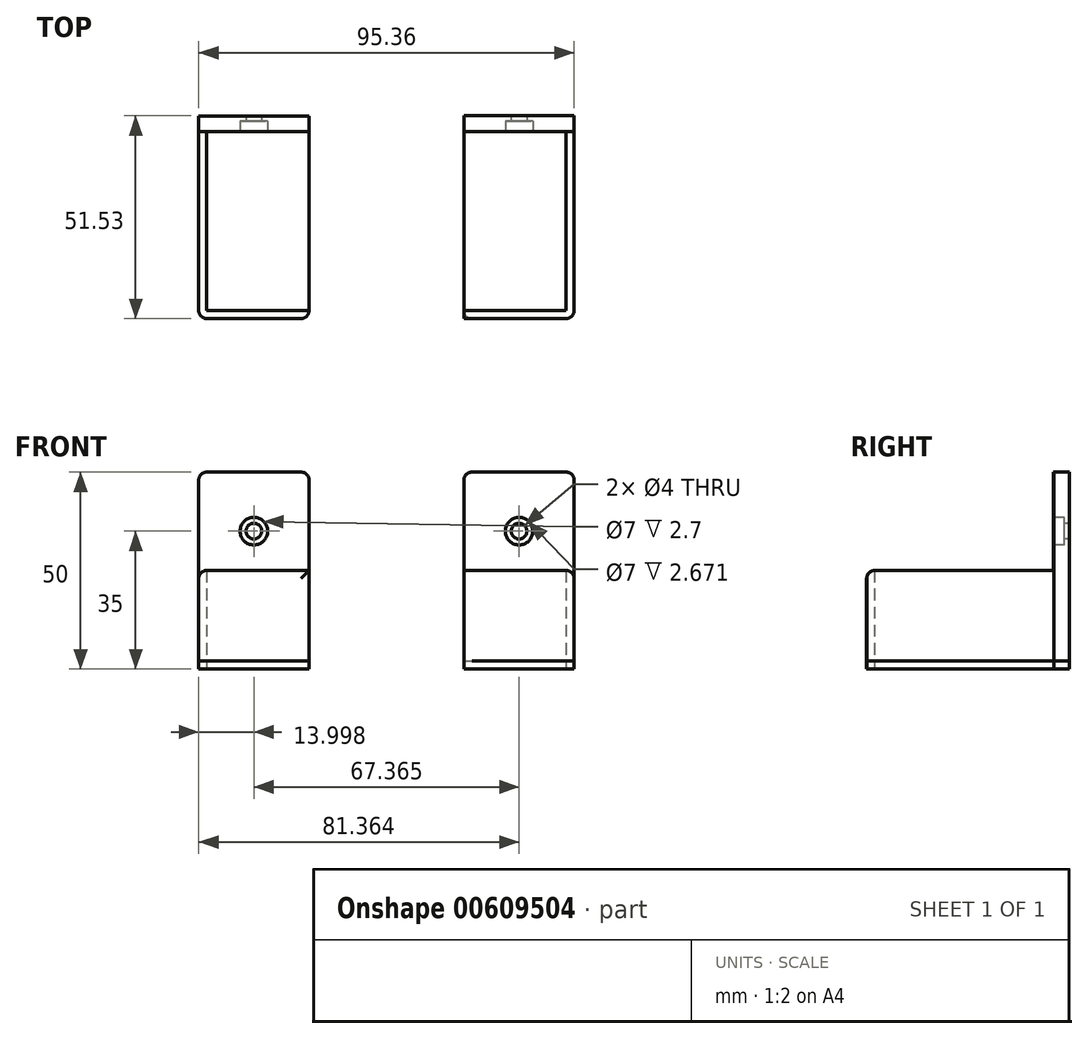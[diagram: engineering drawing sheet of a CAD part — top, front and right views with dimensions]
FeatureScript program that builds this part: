
annotation { "Feature Type Name" : "Feature", "Feature Type Description" : "" }
export const myFeature = defineFeature(function(context is Context, id is Id, definition is map)
    precondition{}
    {
        {
            var Q0;
            Q0=qCreatedBy(makeId("Top.planeOp"),FACE);
            var sketch = newSketch(context, id + "F0", { "sketchPlane" : qUnion([Q0])});
            skLineSegment(sketch, "E0.bottom", {"start": v(17.3, 23.4) * mm, "end": v(45.3, 23.4) * mm});
            skLineSegment(sketch, "E0.top", {"start": v(17.3, -28.1) * mm, "end": v(45.3, -28.1) * mm});
            skLineSegment(sketch, "E0.left", {"start": v(17.3, 23.4) * mm, "end": v(17.3, -28.1) * mm});
            skLineSegment(sketch, "E0.right", {"start": v(45.3, 23.4) * mm, "end": v(45.3, -28.1) * mm});
            skSolve(sketch);
        }
        {
            var Q0;
            Q0=qCreatedBy(makeId("Top.planeOp"),FACE);
            var sketch = newSketch(context, id + "F1", { "sketchPlane" : qUnion([Q0])});
            skLineSegment(sketch, "E1.bottom", {"start": v(-50.07, 23.37) * mm, "end": v(-22.07, 23.37) * mm});
            skLineSegment(sketch, "E1.top", {"start": v(-50.07, -28.13) * mm, "end": v(-22.07, -28.13) * mm});
            skLineSegment(sketch, "E1.left", {"start": v(-50.07, 23.37) * mm, "end": v(-50.07, -28.13) * mm});
            skLineSegment(sketch, "E1.right", {"start": v(-22.07, 23.37) * mm, "end": v(-22.07, -28.13) * mm});
            skSolve(sketch);
        }
        {
            var Q0;
            Q0=makeQuery(id+"F0.imprint","IMPRINT",FACE,{"disambiguationData":[TD([[makeQuery(id+"F0.imprint","IMPRINT",EDGE,{"derivedFrom":sQuery(id+"F0.wireOp",EDGE,"E0.bottom")}),-1.0]])]});
            var sketch = newSketch(context, id + "F2", { "sketchPlane" : qUnion([Q0])});
            skLineSegment(sketch, "E2.bottom", {"start": v(17.3, 23.4) * mm, "end": v(45.3, 23.4) * mm});
            skLineSegment(sketch, "E2.top", {"start": v(17.3, 19.4) * mm, "end": v(45.3, 19.4) * mm});
            skLineSegment(sketch, "E2.left", {"start": v(17.3, 23.4) * mm, "end": v(17.3, 19.4) * mm});
            skLineSegment(sketch, "E2.right", {"start": v(45.3, 23.4) * mm, "end": v(45.3, 19.4) * mm});
            skLineSegment(sketch, "E3.bottom", {"start": v(-50.07, 23.37) * mm, "end": v(-22.07, 23.37) * mm});
            skLineSegment(sketch, "E3.top", {"start": v(-50.07, 19.37) * mm, "end": v(-22.07, 19.37) * mm});
            skLineSegment(sketch, "E3.left", {"start": v(-50.07, 23.37) * mm, "end": v(-50.07, 19.37) * mm});
            skLineSegment(sketch, "E3.right", {"start": v(-22.07, 23.37) * mm, "end": v(-22.07, 19.37) * mm});
            skSolve(sketch);
        }
        {
            var Q0;
            Q0=makeQuery(id+"F1.imprint","IMPRINT",FACE,{"disambiguationData":[TD([[makeQuery(id+"F1.imprint","IMPRINT",EDGE,{"derivedFrom":sQuery(id+"F1.wireOp",EDGE,"E1.bottom")}),-1.0]])]});
            var sketch = newSketch(context, id + "F3", { "sketchPlane" : qUnion([Q0])});
            skLineSegment(sketch, "E4.bottom", {"start": v(-50.07, 19.37) * mm, "end": v(-48.07, 19.37) * mm});
            skLineSegment(sketch, "E4.top", {"start": v(-50.07, -28.13) * mm, "end": v(-48.07, -28.13) * mm});
            skLineSegment(sketch, "E4.left", {"start": v(-50.07, 19.37) * mm, "end": v(-50.07, -28.13) * mm});
            skLineSegment(sketch, "E4.right", {"start": v(-48.07, 19.37) * mm, "end": v(-48.07, -28.13) * mm});
            skLineSegment(sketch, "E5.bottom", {"start": v(45.3, 19.4) * mm, "end": v(43.3, 19.4) * mm});
            skLineSegment(sketch, "E5.top", {"start": v(45.3, -28.1) * mm, "end": v(43.3, -28.1) * mm});
            skLineSegment(sketch, "E5.left", {"start": v(45.3, 19.4) * mm, "end": v(45.3, -28.1) * mm});
            skLineSegment(sketch, "E5.right", {"start": v(43.3, 19.4) * mm, "end": v(43.3, -28.1) * mm});
            skLineSegment(sketch, "E6.bottom", {"start": v(-22.07, -28.13) * mm, "end": v(-48.07, -28.13) * mm});
            skLineSegment(sketch, "E6.top", {"start": v(-22.07, -26.13) * mm, "end": v(-48.07, -26.13) * mm});
            skLineSegment(sketch, "E6.left", {"start": v(-22.07, -28.13) * mm, "end": v(-22.07, -26.13) * mm});
            skLineSegment(sketch, "E6.right", {"start": v(-48.07, -28.13) * mm, "end": v(-48.07, -26.13) * mm});
            skLineSegment(sketch, "E7.bottom", {"start": v(17.3, -28.1) * mm, "end": v(43.3, -28.1) * mm});
            skLineSegment(sketch, "E7.top", {"start": v(17.3, -26.1) * mm, "end": v(43.3, -26.1) * mm});
            skLineSegment(sketch, "E7.left", {"start": v(17.3, -28.1) * mm, "end": v(17.3, -26.1) * mm});
            skLineSegment(sketch, "E7.right", {"start": v(43.3, -28.1) * mm, "end": v(43.3, -26.1) * mm});
            skSolve(sketch);
        }
        {
            var Q0;
            Q0 = qSketchRegion(id + "F0", true);
            var Q1;
            Q1 = qSketchRegion(id + "F1", true);
            extrude(context, id + "F4", {"entities" : qUnion([Q0, Q1]), "depth" : 2 * mm, "offsetDistance" : 25 * mm});
        }
        {
            var Q0;
            Q0 = qSketchRegion(id + "F2", true);
            extrude(context, id + "F5", {"entities" : qUnion([Q0]), "depth" : 50 * mm, "offsetDistance" : 25 * mm});
        }
        {
            var Q0;
            Q0 = qSketchRegion(id + "F3", true);
            extrude(context, id + "F6", {"entities" : qUnion([Q0]), "depth" : 25 * mm, "offsetDistance" : 25 * mm});
        }
        {
            var Q0;
            Q0=makeQuery(id+"F5.opExtrude","SWEPT_FACE",FACE,{"disambiguationData":[OSD([sQuery(id+"F2.wireOp",EDGE,"E3.top")])]});
            var sketch = newSketch(context, id + "F7", { "sketchPlane" : qUnion([Q0])});
            skCircle(sketch, "E8", {"center": v(-36.07, 35) * mm, "radius": 2 * mm});
            skCircle(sketch, "E9", {"center": v(31.3, 35) * mm, "radius": 2 * mm});
            skSolve(sketch);
        }
        {
            var Q0;
            Q0=makeQuery(id+"F7.imprint","IMPRINT",FACE,{"disambiguationData":[TD([[makeQuery(id+"F7.imprint","IMPRINT",EDGE,{"derivedFrom":sQuery(id+"F7.wireOp",EDGE,"E8")}),-1.0]])]});
            var sketch = newSketch(context, id + "F8", { "sketchPlane" : qUnion([Q0])});
            skCircle(sketch, "E10", {"center": v(-36.07, 35) * mm, "radius": 3.5 * mm});
            skCircle(sketch, "E11", {"center": v(31.3, 35) * mm, "radius": 3.5 * mm});
            skSolve(sketch);
        }
        {
            var Q0;
            Q0 = qSketchRegion(id + "F7", true);
            extrude(context, id + "F9", {"entities" : qUnion([Q0]), "operationType" : NewBodyOperationType.REMOVE, "oppositeDirection" : true, "depth" : 6 * mm, "offsetDistance" : 25 * mm});
        }
        {
            var Q0;
            Q0 = qSketchRegion(id + "F8", true);
            extrude(context, id + "F10", {"entities" : qUnion([Q0]), "operationType" : NewBodyOperationType.REMOVE, "oppositeDirection" : true, "depth" : 2.7 * mm, "offsetDistance" : 25 * mm});
        }
        {
            var Q0;
            Q0=makeQuery(id+"F5.opExtrude","CAP_EDGE",EDGE,{"disambiguationData":[OSD([sQuery(id+"F2.wireOp",EDGE,"E3.left")])],"isStart":false});
            var Q1;
            Q1=makeQuery(id+"F6.opExtrude","CAP_EDGE",EDGE,{"disambiguationData":[OSD([sQuery(id+"F3.wireOp",EDGE,"E4.left")])],"isStart":false});
            var Q2;
            Q2=makeQuery(id+"F6.opExtrude","CAP_EDGE",EDGE,{"disambiguationData":[OSD([sQuery(id+"F3.wireOp",EDGE,"E4.top"),sQuery(id+"F3.wireOp",EDGE,"E6.bottom")])],"isStart":false});
            var Q3;
            Q3=makeQuery(id+"F5.opExtrude","CAP_EDGE",EDGE,{"disambiguationData":[OSD([sQuery(id+"F2.wireOp",EDGE,"E3.right")])],"isStart":false});
            var Q4;
            Q4=makeQuery(id+"F6.opExtrude","CAP_EDGE",EDGE,{"disambiguationData":[OSD([sQuery(id+"F3.wireOp",EDGE,"E5.top"),sQuery(id+"F3.wireOp",EDGE,"E7.bottom")])],"isStart":false});
            var Q5;
            Q5=makeQuery(id+"F6.opExtrude","CAP_EDGE",EDGE,{"disambiguationData":[OSD([sQuery(id+"F3.wireOp",EDGE,"E5.left")])],"isStart":false});
            var Q6;
            Q6=makeQuery(id+"F5.opExtrude","CAP_EDGE",EDGE,{"disambiguationData":[OSD([sQuery(id+"F2.wireOp",EDGE,"E2.right")])],"isStart":false});
            var Q7;
            Q7=makeQuery(id+"F5.opExtrude","CAP_EDGE",EDGE,{"disambiguationData":[OSD([sQuery(id+"F2.wireOp",EDGE,"E2.left")])],"isStart":false});
            var Q8;
            Q8=makeQuery(id+"F6.opExtrude","SWEPT_EDGE",EDGE,{"disambiguationData":[OSD([sQuery(id+"F3.wireOp",EDGE,"E6.bottom"),sQuery(id+"F3.wireOp",EDGE,"E6.left")])]});
            var Q9;
            Q9=makeQuery(id+"F6.opExtrude","SWEPT_EDGE",EDGE,{"disambiguationData":[OSD([sQuery(id+"F3.wireOp",EDGE,"E4.top"),sQuery(id+"F3.wireOp",EDGE,"E4.left")])]});
            var Q10;
            Q10=makeQuery(id+"F4.opExtrude","SWEPT_EDGE",EDGE,{"disambiguationData":[OSD([sQuery(id+"F0.wireOp",EDGE,"E0.top"),sQuery(id+"F0.wireOp",EDGE,"E0.left")])]});
            var Q11;
            Q11=makeQuery(id+"F4.opExtrude","SWEPT_EDGE",EDGE,{"disambiguationData":[OSD([sQuery(id+"F0.wireOp",EDGE,"E0.top"),sQuery(id+"F0.wireOp",EDGE,"E0.right")])]});
            var Q12;
            Q12=makeQuery(id+"F6.opExtrude","SWEPT_EDGE",EDGE,{"disambiguationData":[OSD([sQuery(id+"F3.wireOp",EDGE,"E5.top"),sQuery(id+"F3.wireOp",EDGE,"E5.left")])]});
            var Q13;
            Q13=makeQuery(id+"F4.opExtrude","SWEPT_EDGE",EDGE,{"disambiguationData":[OSD([sQuery(id+"F1.wireOp",EDGE,"E1.top"),sQuery(id+"F1.wireOp",EDGE,"E1.right")])]});
            var Q14;
            Q14=makeQuery(id+"F4.opExtrude","SWEPT_EDGE",EDGE,{"disambiguationData":[OSD([sQuery(id+"F1.wireOp",EDGE,"E1.top"),sQuery(id+"F1.wireOp",EDGE,"E1.left")])]});
            fillet(context, id + "F11", {"entities" : qUnion([Q0, Q1, Q2, Q3, Q4, Q5, Q6, Q7, Q8, Q9, Q10, Q11, Q12, Q13, Q14]), "radius" : 2 * mm, "tangentPropagation" : true, "allowEdgeOverflow" : false});
        }
    });
